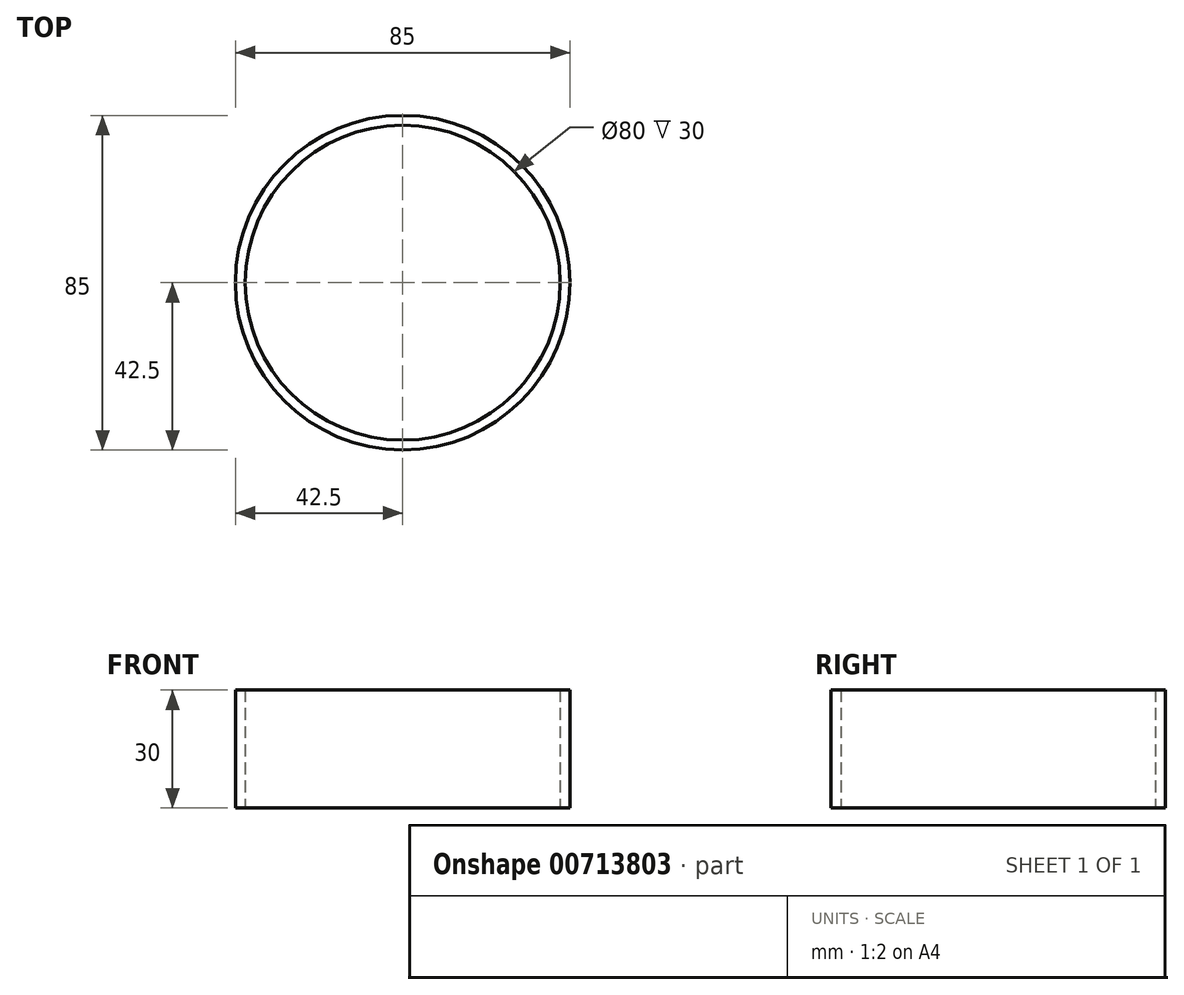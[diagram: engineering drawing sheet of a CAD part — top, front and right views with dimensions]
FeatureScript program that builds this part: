
annotation { "Feature Type Name" : "Feature", "Feature Type Description" : "" }
export const myFeature = defineFeature(function(context is Context, id is Id, definition is map)
    precondition{}
    {
        {
            var Q0;
            Q0=qCreatedBy(makeId("Top.planeOp"),FACE);
            var sketch = newSketch(context, id + "F0", { "sketchPlane" : qUnion([Q0])});
            skCircle(sketch, "E0", {"center": v(0, 0) * mm, "radius": 40 * mm});
            skCircle(sketch, "E1", {"center": v(0, 0) * mm, "radius": 42.5 * mm});
            skSolve(sketch);
        }
        {
            var Q0;
            Q0 = qSketchRegion(id + "F0", true);
            extrude(context, id + "F1", {"entities" : qUnion([Q0]), "depth" : 30 * mm, "offsetDistance" : 25 * mm});
        }
    });
